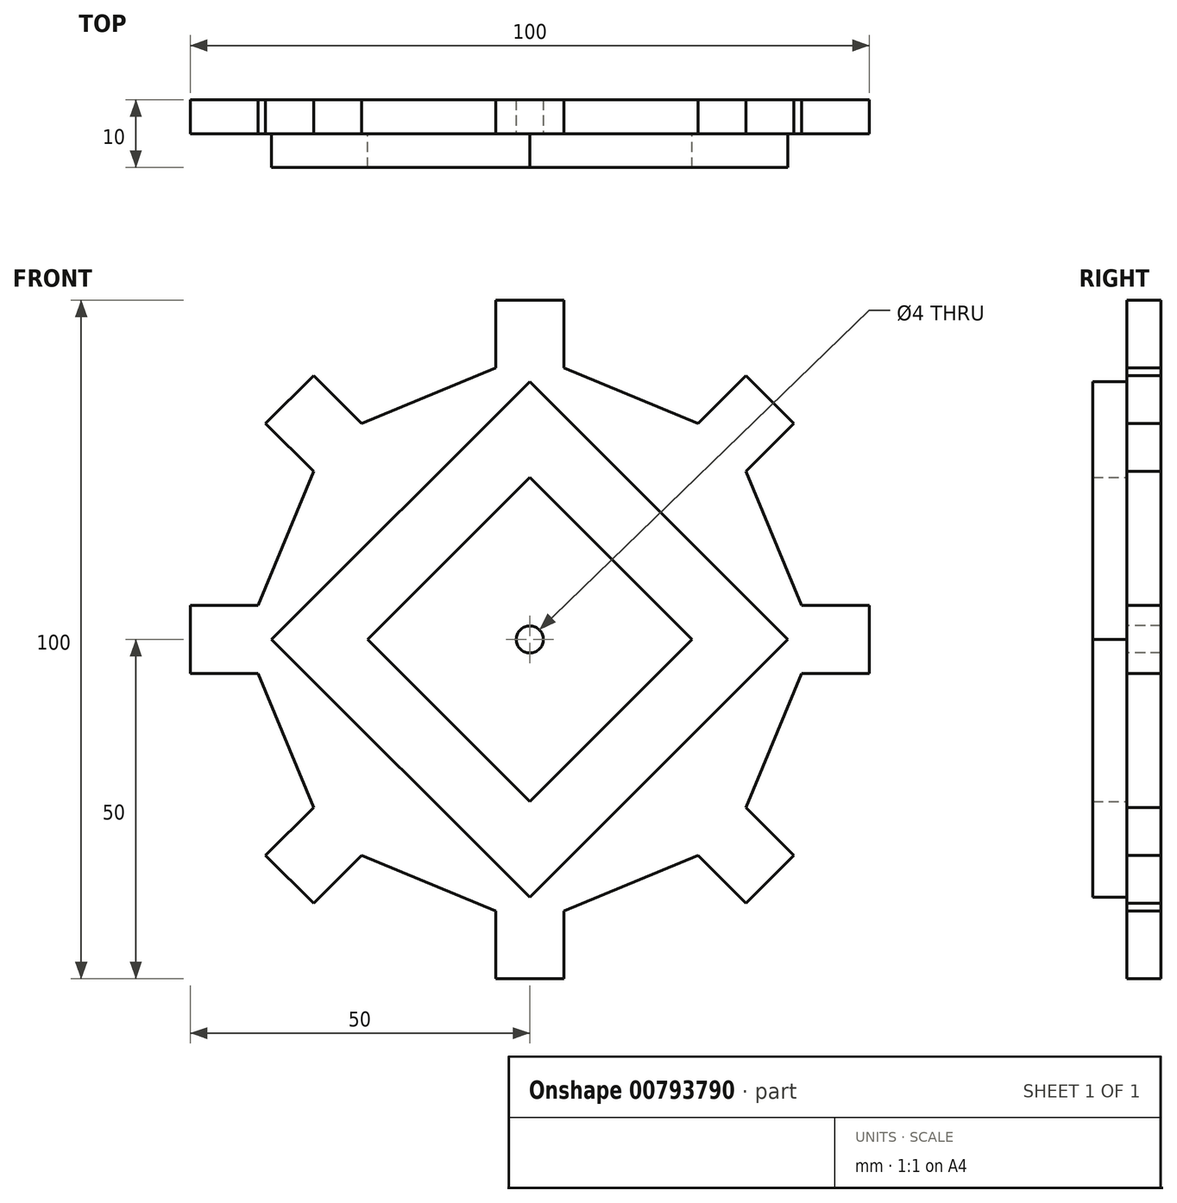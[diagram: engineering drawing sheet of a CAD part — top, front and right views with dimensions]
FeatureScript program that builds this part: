
annotation { "Feature Type Name" : "Feature", "Feature Type Description" : "" }
export const myFeature = defineFeature(function(context is Context, id is Id, definition is map)
    precondition{}
    {
        {
            var Q0;
            Q0=qCreatedBy(makeId("Front.planeOp"),FACE);
            var sketch = newSketch(context, id + "F0", { "sketchPlane" : qUnion([Q0])});
            skLineSegment(sketch, "E0.bottom", {"start": v(5, -50) * mm, "end": v(-5, -50) * mm});
            skLineSegment(sketch, "E0.top", {"start": v(5, 50) * mm, "end": v(-5, 50) * mm});
            skLineSegment(sketch, "E0.left", {"start": v(5, -50) * mm, "end": v(5, 50) * mm});
            skLineSegment(sketch, "E0.right", {"start": v(-5, -50) * mm, "end": v(-5, 50) * mm});
            skPoint(sketch, "E0.middle", {"position": v(0, 0) * mm});
            skLineSegment(sketch, "E1.bottom", {"start": v(50, -5) * mm, "end": v(-50, -5) * mm});
            skLineSegment(sketch, "E1.top", {"start": v(50, 5) * mm, "end": v(-50, 5) * mm});
            skLineSegment(sketch, "E1.left", {"start": v(50, -5) * mm, "end": v(50, 5) * mm});
            skLineSegment(sketch, "E1.right", {"start": v(-50, -5) * mm, "end": v(-50, 5) * mm});
            skLineSegment(sketch, "E2", {"start": v(-5, -5) * mm, "end": v(5, 5) * mm});
            skLineSegment(sketch, "E3", {"start": v(0, 0) * mm, "end": v(-3.54, -3.54) * mm});
            skLineSegment(sketch, "E4", {"start": v(0, 0) * mm, "end": v(3.54, 3.54) * mm});
            skLineSegment(sketch, "E5", {"start": v(3.54, 3.54) * mm, "end": v(-31.82, 38.9) * mm});
            skLineSegment(sketch, "E6", {"start": v(-31.82, 38.9) * mm, "end": v(-38.9, 31.82) * mm});
            skLineSegment(sketch, "E7", {"start": v(-38.9, 31.82) * mm, "end": v(-3.54, -3.54) * mm});
            skLineSegment(sketch, "E8.MirrorCS", {"start": v(3.54, 3.54) * mm, "end": v(38.9, -31.82) * mm});
            skLineSegment(sketch, "E9.MirrorCS", {"start": v(31.82, -38.9) * mm, "end": v(-3.54, -3.54) * mm});
            skLineSegment(sketch, "E10.MirrorCS", {"start": v(38.9, -31.82) * mm, "end": v(31.82, -38.9) * mm});
            skLineSegment(sketch, "E11", {"start": v(-5, 5) * mm, "end": v(5, -5) * mm});
            skLineSegment(sketch, "E12", {"start": v(0, 0) * mm, "end": v(-3.54, 3.54) * mm});
            skLineSegment(sketch, "E13", {"start": v(0, 0) * mm, "end": v(3.54, -3.54) * mm});
            skLineSegment(sketch, "E14", {"start": v(3.54, -3.54) * mm, "end": v(-31.82, -38.9) * mm});
            skLineSegment(sketch, "E15", {"start": v(-31.82, -38.9) * mm, "end": v(-38.9, -31.82) * mm});
            skLineSegment(sketch, "E16", {"start": v(-38.9, -31.82) * mm, "end": v(-3.54, 3.54) * mm});
            skLineSegment(sketch, "E17.MirrorCS", {"start": v(3.54, -3.54) * mm, "end": v(38.9, 31.82) * mm});
            skLineSegment(sketch, "E18.MirrorCS", {"start": v(31.82, 38.9) * mm, "end": v(-3.54, 3.54) * mm});
            skLineSegment(sketch, "E19.MirrorCS", {"start": v(38.9, 31.82) * mm, "end": v(31.82, 38.9) * mm});
            skLineSegment(sketch, "E20", {"start": v(-5, 50) * mm, "end": v(-5, 40) * mm});
            skLineSegment(sketch, "E21", {"start": v(-5, 40) * mm, "end": v(5, 40) * mm});
            skLineSegment(sketch, "E22", {"start": v(-38.9, 31.82) * mm, "end": v(-31.82, 24.75) * mm});
            skLineSegment(sketch, "E23", {"start": v(-31.82, 24.75) * mm, "end": v(-24.75, 31.82) * mm});
            skLineSegment(sketch, "E24", {"start": v(-50, -5) * mm, "end": v(-40, -5) * mm});
            skLineSegment(sketch, "E25", {"start": v(-40, -5) * mm, "end": v(-40, 5) * mm});
            skLineSegment(sketch, "E26", {"start": v(-31.82, -38.9) * mm, "end": v(-24.75, -31.82) * mm});
            skLineSegment(sketch, "E27", {"start": v(-24.75, -31.82) * mm, "end": v(-31.82, -24.75) * mm});
            skLineSegment(sketch, "E28", {"start": v(5, -50) * mm, "end": v(5, -40) * mm});
            skLineSegment(sketch, "E29", {"start": v(5, -40) * mm, "end": v(-5, -40) * mm});
            skLineSegment(sketch, "E30", {"start": v(38.9, -31.82) * mm, "end": v(31.82, -24.75) * mm});
            skLineSegment(sketch, "E31", {"start": v(31.82, -24.75) * mm, "end": v(24.75, -31.82) * mm});
            skLineSegment(sketch, "E32", {"start": v(50, -5) * mm, "end": v(40, -5) * mm});
            skLineSegment(sketch, "E33", {"start": v(40, -5) * mm, "end": v(40, 5) * mm});
            skLineSegment(sketch, "E34", {"start": v(38.9, 31.82) * mm, "end": v(31.82, 24.75) * mm});
            skLineSegment(sketch, "E35", {"start": v(31.82, 24.75) * mm, "end": v(24.75, 31.82) * mm});
            skLineSegment(sketch, "E36", {"start": v(24.75, 31.82) * mm, "end": v(5, 40) * mm});
            skLineSegment(sketch, "E37", {"start": v(-5, 40) * mm, "end": v(-24.75, 31.82) * mm});
            skLineSegment(sketch, "E38", {"start": v(-31.82, 24.75) * mm, "end": v(-40, 5) * mm});
            skLineSegment(sketch, "E39", {"start": v(-40, -5) * mm, "end": v(-31.82, -24.75) * mm});
            skLineSegment(sketch, "E40", {"start": v(-24.75, -31.82) * mm, "end": v(-5, -40) * mm});
            skLineSegment(sketch, "E41", {"start": v(5, -40) * mm, "end": v(24.75, -31.82) * mm});
            skLineSegment(sketch, "E42", {"start": v(31.82, -24.75) * mm, "end": v(40, -5) * mm});
            skLineSegment(sketch, "E43", {"start": v(40, 5) * mm, "end": v(31.82, 24.75) * mm});
            skSolve(sketch);
        }
        {
            var Q0;
            {var subQ3=sQuery(id+"F0.wireOp",EDGE,"E40");Q0=makeQuery(id+"F0.imprint","IMPRINT",FACE,{"disambiguationData":[TD([[makeQuery(id+"F0.imprint","IMPRINT",EDGE,{"derivedFrom":subQ3}),1.0]])]});}
            var Q1;
            {var subQ3=sQuery(id+"F0.wireOp",EDGE,"E37");Q1=makeQuery(id+"F0.imprint","IMPRINT",FACE,{"disambiguationData":[TD([[makeQuery(id+"F0.imprint","IMPRINT",EDGE,{"derivedFrom":subQ3}),1.0]])]});}
            var Q2;
            {var subQ3=sQuery(id+"F0.wireOp",EDGE,"E36");Q2=makeQuery(id+"F0.imprint","IMPRINT",FACE,{"disambiguationData":[TD([[makeQuery(id+"F0.imprint","IMPRINT",EDGE,{"derivedFrom":subQ3}),1.0]])]});}
            var Q3;
            {var subQ0=sQuery(id+"F0.wireOp",EDGE,"E15");Q3=makeQuery(id+"F0.imprint","IMPRINT",FACE,{"disambiguationData":[TD([[makeQuery(id+"F0.imprint","IMPRINT",EDGE,{"derivedFrom":subQ0}),-1.0]])]});}
            var Q4;
            {var subQ0=sQuery(id+"F0.wireOp",EDGE,"E19.MirrorCS");Q4=makeQuery(id+"F0.imprint","IMPRINT",FACE,{"disambiguationData":[TD([[makeQuery(id+"F0.imprint","IMPRINT",EDGE,{"derivedFrom":subQ0}),1.0]])]});}
            var Q5;
            {var subQ0=sQuery(id+"F0.wireOp",EDGE,"E41");Q5=makeQuery(id+"F0.imprint","IMPRINT",FACE,{"disambiguationData":[TD([[makeQuery(id+"F0.imprint","IMPRINT",EDGE,{"derivedFrom":subQ0}),1.0]])]});}
            var Q6;
            {var subQ0=sQuery(id+"F0.wireOp",EDGE,"E10.MirrorCS");Q6=makeQuery(id+"F0.imprint","IMPRINT",FACE,{"disambiguationData":[TD([[makeQuery(id+"F0.imprint","IMPRINT",EDGE,{"derivedFrom":subQ0}),-1.0]])]});}
            var Q7;
            {var subQ3=sQuery(id+"F0.wireOp",EDGE,"E39");Q7=makeQuery(id+"F0.imprint","IMPRINT",FACE,{"disambiguationData":[TD([[makeQuery(id+"F0.imprint","IMPRINT",EDGE,{"derivedFrom":subQ3}),1.0]])]});}
            var Q8;
            {var subQ3=sQuery(id+"F0.wireOp",EDGE,"E23");Q8=makeQuery(id+"F0.imprint","IMPRINT",FACE,{"disambiguationData":[TD([[makeQuery(id+"F0.imprint","IMPRINT",EDGE,{"derivedFrom":subQ3}),-1.0]])]});}
            var Q9;
            {var subQ0=sQuery(id+"F0.wireOp",EDGE,"E6");Q9=makeQuery(id+"F0.imprint","IMPRINT",FACE,{"disambiguationData":[TD([[makeQuery(id+"F0.imprint","IMPRINT",EDGE,{"derivedFrom":subQ0}),1.0]])]});}
            var Q10;
            {var subQ3=sQuery(id+"F0.wireOp",EDGE,"E38");Q10=makeQuery(id+"F0.imprint","IMPRINT",FACE,{"disambiguationData":[TD([[makeQuery(id+"F0.imprint","IMPRINT",EDGE,{"derivedFrom":subQ3}),1.0]])]});}
            var Q11;
            {var subQ0=sQuery(id+"F0.wireOp",EDGE,"E1.right");Q11=makeQuery(id+"F0.imprint","IMPRINT",FACE,{"disambiguationData":[TD([[makeQuery(id+"F0.imprint","IMPRINT",EDGE,{"derivedFrom":subQ0}),-1.0]])]});}
            var Q12;
            {var subQ0=sQuery(id+"F0.wireOp",EDGE,"E7");var subQ1=sQuery(id+"F0.wireOp",EDGE,"E0.right");var subQ2=makeQuery(id+"F0.imprint","INTERSECT",VERTEX,{"derivedFrom":[subQ1,subQ0]});Q12=makeQuery(id+"F0.imprint","IMPRINT",FACE,{"disambiguationData":[TD([[makeQuery(id+"F0.imprint","IMPRINT",EDGE,{"disambiguationData":[TD([[subQ2,1.0]])],"derivedFrom":subQ0}),-1.0]])]});}
            var Q13;
            {var subQ0=sQuery(id+"F0.wireOp",EDGE,"E1.left");Q13=makeQuery(id+"F0.imprint","IMPRINT",FACE,{"disambiguationData":[TD([[makeQuery(id+"F0.imprint","IMPRINT",EDGE,{"derivedFrom":subQ0}),1.0]])]});}
            var Q14;
            {var subQ0=sQuery(id+"F0.wireOp",EDGE,"E17.MirrorCS");var subQ1=sQuery(id+"F0.wireOp",EDGE,"E0.left");var subQ2=makeQuery(id+"F0.imprint","INTERSECT",VERTEX,{"derivedFrom":[subQ1,subQ0]});Q14=makeQuery(id+"F0.imprint","IMPRINT",FACE,{"disambiguationData":[TD([[makeQuery(id+"F0.imprint","IMPRINT",EDGE,{"disambiguationData":[TD([[subQ2,-1.0]])],"derivedFrom":subQ1}),-1.0]])]});}
            var Q15;
            {var subQ0=sQuery(id+"F0.wireOp",EDGE,"E0.top");Q15=makeQuery(id+"F0.imprint","IMPRINT",FACE,{"disambiguationData":[TD([[makeQuery(id+"F0.imprint","IMPRINT",EDGE,{"derivedFrom":subQ0}),1.0]])]});}
            var Q16;
            {var subQ3=sQuery(id+"F0.wireOp",EDGE,"E17.MirrorCS");var subQ6=sQuery(id+"F0.wireOp",EDGE,"E0.left");var subQ9=makeQuery(id+"F0.imprint","INTERSECT",VERTEX,{"derivedFrom":[subQ6,subQ3]});Q16=makeQuery(id+"F0.imprint","IMPRINT",FACE,{"disambiguationData":[TD([[makeQuery(id+"F0.imprint","IMPRINT",EDGE,{"disambiguationData":[TD([[subQ9,-1.0]])],"derivedFrom":subQ6}),1.0]])]});}
            var Q17;
            {var subQ7=sQuery(id+"F0.wireOp",EDGE,"E29");Q17=makeQuery(id+"F0.imprint","IMPRINT",FACE,{"disambiguationData":[TD([[makeQuery(id+"F0.imprint","IMPRINT",EDGE,{"derivedFrom":subQ7}),-1.0]])]});}
            var Q18;
            {var subQ0=sQuery(id+"F0.wireOp",EDGE,"E0.bottom");Q18=makeQuery(id+"F0.imprint","IMPRINT",FACE,{"disambiguationData":[TD([[makeQuery(id+"F0.imprint","IMPRINT",EDGE,{"derivedFrom":subQ0}),-1.0]])]});}
            var Q19;
            {var subQ0=sQuery(id+"F0.wireOp",EDGE,"E9.MirrorCS");var subQ1=sQuery(id+"F0.wireOp",EDGE,"E0.left");var subQ2=makeQuery(id+"F0.imprint","INTERSECT",VERTEX,{"derivedFrom":[subQ1,subQ0]});Q19=makeQuery(id+"F0.imprint","IMPRINT",FACE,{"disambiguationData":[TD([[makeQuery(id+"F0.imprint","IMPRINT",EDGE,{"disambiguationData":[TD([[subQ2,-1.0]])],"derivedFrom":subQ0}),-1.0]])]});}
            var Q20;
            {var subQ7=sQuery(id+"F0.wireOp",EDGE,"E33");Q20=makeQuery(id+"F0.imprint","IMPRINT",FACE,{"disambiguationData":[TD([[makeQuery(id+"F0.imprint","IMPRINT",EDGE,{"derivedFrom":subQ7}),1.0]])]});}
            var Q21;
            {var subQ0=sQuery(id+"F0.wireOp",EDGE,"E8.MirrorCS");var subQ1=sQuery(id+"F0.wireOp",EDGE,"E0.left");var subQ2=makeQuery(id+"F0.imprint","INTERSECT",VERTEX,{"derivedFrom":[subQ1,subQ0]});Q21=makeQuery(id+"F0.imprint","IMPRINT",FACE,{"disambiguationData":[TD([[makeQuery(id+"F0.imprint","IMPRINT",EDGE,{"disambiguationData":[TD([[subQ2,-1.0]])],"derivedFrom":subQ0}),1.0]])]});}
            var Q22;
            {var subQ0=sQuery(id+"F0.wireOp",EDGE,"E31");Q22=makeQuery(id+"F0.imprint","IMPRINT",FACE,{"disambiguationData":[TD([[makeQuery(id+"F0.imprint","IMPRINT",EDGE,{"derivedFrom":subQ0}),-1.0]])]});}
            var Q23;
            {var subQ0=sQuery(id+"F0.wireOp",EDGE,"E14");var subQ1=sQuery(id+"F0.wireOp",EDGE,"E1.bottom");var subQ2=makeQuery(id+"F0.imprint","INTERSECT",VERTEX,{"derivedFrom":[subQ1,subQ0]});Q23=makeQuery(id+"F0.imprint","IMPRINT",FACE,{"disambiguationData":[TD([[makeQuery(id+"F0.imprint","IMPRINT",EDGE,{"disambiguationData":[TD([[subQ2,-1.0]])],"derivedFrom":subQ1}),1.0]])]});}
            var Q24;
            {var subQ3=sQuery(id+"F0.wireOp",EDGE,"E35");Q24=makeQuery(id+"F0.imprint","IMPRINT",FACE,{"disambiguationData":[TD([[makeQuery(id+"F0.imprint","IMPRINT",EDGE,{"derivedFrom":subQ3}),1.0]])]});}
            var Q25;
            {var subQ7=sQuery(id+"F0.wireOp",EDGE,"E25");Q25=makeQuery(id+"F0.imprint","IMPRINT",FACE,{"disambiguationData":[TD([[makeQuery(id+"F0.imprint","IMPRINT",EDGE,{"derivedFrom":subQ7}),-1.0]])]});}
            var Q26;
            {var subQ0=sQuery(id+"F0.wireOp",EDGE,"E1.bottom");var subQ5=sQuery(id+"F0.wireOp",EDGE,"E9.MirrorCS");var subQ6=makeQuery(id+"F0.imprint","INTERSECT",VERTEX,{"derivedFrom":[subQ0,subQ5]});Q26=makeQuery(id+"F0.imprint","IMPRINT",FACE,{"disambiguationData":[TD([[makeQuery(id+"F0.imprint","IMPRINT",EDGE,{"disambiguationData":[TD([[subQ6,1.0]])],"derivedFrom":subQ5}),1.0]])]});}
            var Q27;
            {var subQ3=sQuery(id+"F0.wireOp",EDGE,"E1.bottom");var subQ5=sQuery(id+"F0.wireOp",EDGE,"E8.MirrorCS");var subQ6=makeQuery(id+"F0.imprint","INTERSECT",VERTEX,{"derivedFrom":[subQ3,subQ5]});Q27=makeQuery(id+"F0.imprint","IMPRINT",FACE,{"disambiguationData":[TD([[makeQuery(id+"F0.imprint","IMPRINT",EDGE,{"disambiguationData":[TD([[subQ6,1.0]])],"derivedFrom":subQ5}),-1.0]])]});}
            var Q28;
            {var subQ3=sQuery(id+"F0.wireOp",EDGE,"E42");Q28=makeQuery(id+"F0.imprint","IMPRINT",FACE,{"disambiguationData":[TD([[makeQuery(id+"F0.imprint","IMPRINT",EDGE,{"derivedFrom":subQ3}),1.0]])]});}
            var Q29;
            {var subQ3=sQuery(id+"F0.wireOp",EDGE,"E43");Q29=makeQuery(id+"F0.imprint","IMPRINT",FACE,{"disambiguationData":[TD([[makeQuery(id+"F0.imprint","IMPRINT",EDGE,{"derivedFrom":subQ3}),1.0]])]});}
            var Q30;
            {var subQ3=sQuery(id+"F0.wireOp",EDGE,"E1.bottom");var subQ7=sQuery(id+"F0.wireOp",EDGE,"E14");var subQ9=makeQuery(id+"F0.imprint","INTERSECT",VERTEX,{"derivedFrom":[subQ3,subQ7]});Q30=makeQuery(id+"F0.imprint","IMPRINT",FACE,{"disambiguationData":[TD([[makeQuery(id+"F0.imprint","IMPRINT",EDGE,{"disambiguationData":[TD([[subQ9,-1.0]])],"derivedFrom":subQ3}),-1.0]])]});}
            var Q31;
            {var subQ7=sQuery(id+"F0.wireOp",EDGE,"E21");Q31=makeQuery(id+"F0.imprint","IMPRINT",FACE,{"disambiguationData":[TD([[makeQuery(id+"F0.imprint","IMPRINT",EDGE,{"derivedFrom":subQ7}),-1.0]])]});}
            var Q32;
            {var subQ0=sQuery(id+"F0.wireOp",EDGE,"E7");var subQ1=sQuery(id+"F0.wireOp",EDGE,"E0.right");var subQ2=makeQuery(id+"F0.imprint","INTERSECT",VERTEX,{"derivedFrom":[subQ1,subQ0]});Q32=makeQuery(id+"F0.imprint","IMPRINT",FACE,{"disambiguationData":[TD([[makeQuery(id+"F0.imprint","IMPRINT",EDGE,{"disambiguationData":[TD([[subQ2,-1.0]])],"derivedFrom":subQ1}),1.0]])]});}
            var Q33;
            {var subQ0=sQuery(id+"F0.wireOp",EDGE,"E1.top");var subQ5=sQuery(id+"F0.wireOp",EDGE,"E7");var subQ6=makeQuery(id+"F0.imprint","INTERSECT",VERTEX,{"derivedFrom":[subQ0,subQ5]});Q33=makeQuery(id+"F0.imprint","IMPRINT",FACE,{"disambiguationData":[TD([[makeQuery(id+"F0.imprint","IMPRINT",EDGE,{"disambiguationData":[TD([[subQ6,-1.0]])],"derivedFrom":subQ5}),1.0]])]});}
            var Q34;
            {var subQ0=sQuery(id+"F0.wireOp",EDGE,"E5");var subQ1=sQuery(id+"F0.wireOp",EDGE,"E1.top");var subQ2=makeQuery(id+"F0.imprint","INTERSECT",VERTEX,{"derivedFrom":[subQ1,subQ0]});Q34=makeQuery(id+"F0.imprint","IMPRINT",FACE,{"disambiguationData":[TD([[makeQuery(id+"F0.imprint","IMPRINT",EDGE,{"disambiguationData":[TD([[subQ2,-1.0]])],"derivedFrom":subQ1}),-1.0]])]});}
            var Q35;
            {var subQ0=sQuery(id+"F0.wireOp",EDGE,"E7");var subQ1=sQuery(id+"F0.wireOp",EDGE,"E0.right");var subQ2=makeQuery(id+"F0.imprint","INTERSECT",VERTEX,{"derivedFrom":[subQ1,subQ0]});Q35=makeQuery(id+"F0.imprint","IMPRINT",FACE,{"disambiguationData":[TD([[makeQuery(id+"F0.imprint","IMPRINT",EDGE,{"disambiguationData":[TD([[subQ2,-1.0]])],"derivedFrom":subQ1}),-1.0]])]});}
            var Q36;
            {var subQ3=sQuery(id+"F0.wireOp",EDGE,"E1.top");var subQ5=sQuery(id+"F0.wireOp",EDGE,"E5");var subQ6=makeQuery(id+"F0.imprint","INTERSECT",VERTEX,{"derivedFrom":[subQ3,subQ5]});Q36=makeQuery(id+"F0.imprint","IMPRINT",FACE,{"disambiguationData":[TD([[makeQuery(id+"F0.imprint","IMPRINT",EDGE,{"disambiguationData":[TD([[subQ6,-1.0]])],"derivedFrom":subQ5}),-1.0]])]});}
            var Q37;
            {var subQ0=sQuery(id+"F0.wireOp",EDGE,"E5");var subQ1=sQuery(id+"F0.wireOp",EDGE,"E0.right");var subQ2=makeQuery(id+"F0.imprint","INTERSECT",VERTEX,{"derivedFrom":[subQ1,subQ0]});Q37=makeQuery(id+"F0.imprint","IMPRINT",FACE,{"disambiguationData":[TD([[makeQuery(id+"F0.imprint","IMPRINT",EDGE,{"disambiguationData":[TD([[subQ2,1.0]])],"derivedFrom":subQ0}),1.0]])]});}
            var Q38;
            {var subQ3=sQuery(id+"F0.wireOp",EDGE,"E27");Q38=makeQuery(id+"F0.imprint","IMPRINT",FACE,{"disambiguationData":[TD([[makeQuery(id+"F0.imprint","IMPRINT",EDGE,{"derivedFrom":subQ3}),-1.0]])]});}
            var Q39;
            {var subQ5=sQuery(id+"F0.wireOp",EDGE,"E5");var subQ6=sQuery(id+"F0.wireOp",EDGE,"E1.top");var subQ7=makeQuery(id+"F0.imprint","INTERSECT",VERTEX,{"derivedFrom":[subQ6,subQ5]});Q39=makeQuery(id+"F0.imprint","IMPRINT",FACE,{"disambiguationData":[TD([[makeQuery(id+"F0.imprint","IMPRINT",EDGE,{"disambiguationData":[TD([[subQ7,-1.0]])],"derivedFrom":subQ6}),1.0]])]});}
            var Q40;
            {var subQ1=sQuery(id+"F0.wireOp",EDGE,"E1.top");var subQ3=sQuery(id+"F0.wireOp",EDGE,"E18.MirrorCS");var subQ4=makeQuery(id+"F0.imprint","INTERSECT",VERTEX,{"derivedFrom":[subQ1,subQ3]});Q40=makeQuery(id+"F0.imprint","IMPRINT",FACE,{"disambiguationData":[TD([[makeQuery(id+"F0.imprint","IMPRINT",EDGE,{"disambiguationData":[TD([[subQ4,-1.0]])],"derivedFrom":subQ1}),1.0]])]});}
            var Q41;
            {var subQ0=sQuery(id+"F0.wireOp",EDGE,"E14");var subQ1=sQuery(id+"F0.wireOp",EDGE,"E1.bottom");var subQ2=makeQuery(id+"F0.imprint","INTERSECT",VERTEX,{"derivedFrom":[subQ1,subQ0]});Q41=makeQuery(id+"F0.imprint","IMPRINT",FACE,{"disambiguationData":[TD([[makeQuery(id+"F0.imprint","IMPRINT",EDGE,{"disambiguationData":[TD([[subQ2,1.0]])],"derivedFrom":subQ1}),-1.0]])]});}
            var Q42;
            {var subQ1=sQuery(id+"F0.wireOp",EDGE,"E0.right");var subQ3=sQuery(id+"F0.wireOp",EDGE,"E16");var subQ4=makeQuery(id+"F0.imprint","INTERSECT",VERTEX,{"derivedFrom":[subQ1,subQ3]});Q42=makeQuery(id+"F0.imprint","IMPRINT",FACE,{"disambiguationData":[TD([[makeQuery(id+"F0.imprint","IMPRINT",EDGE,{"disambiguationData":[TD([[subQ4,-1.0]])],"derivedFrom":subQ1}),-1.0]])]});}
            var Q43;
            {var subQ0=sQuery(id+"F0.wireOp",EDGE,"E17.MirrorCS");var subQ1=sQuery(id+"F0.wireOp",EDGE,"E0.left");var subQ2=makeQuery(id+"F0.imprint","INTERSECT",VERTEX,{"derivedFrom":[subQ1,subQ0]});Q43=makeQuery(id+"F0.imprint","IMPRINT",FACE,{"disambiguationData":[TD([[makeQuery(id+"F0.imprint","IMPRINT",EDGE,{"disambiguationData":[TD([[subQ2,1.0]])],"derivedFrom":subQ1}),1.0]])]});}
            var Q44;
            {var subQ1=sQuery(id+"F0.wireOp",EDGE,"E1.bottom");var subQ3=sQuery(id+"F0.wireOp",EDGE,"E9.MirrorCS");var subQ4=makeQuery(id+"F0.imprint","INTERSECT",VERTEX,{"derivedFrom":[subQ1,subQ3]});Q44=makeQuery(id+"F0.imprint","IMPRINT",FACE,{"disambiguationData":[TD([[makeQuery(id+"F0.imprint","IMPRINT",EDGE,{"disambiguationData":[TD([[subQ4,-1.0]])],"derivedFrom":subQ1}),-1.0]])]});}
            var Q45;
            {var subQ0=sQuery(id+"F0.wireOp",EDGE,"E8.MirrorCS");var subQ1=sQuery(id+"F0.wireOp",EDGE,"E0.left");var subQ2=makeQuery(id+"F0.imprint","INTERSECT",VERTEX,{"derivedFrom":[subQ1,subQ0]});Q45=makeQuery(id+"F0.imprint","IMPRINT",FACE,{"disambiguationData":[TD([[makeQuery(id+"F0.imprint","IMPRINT",EDGE,{"disambiguationData":[TD([[subQ2,-1.0]])],"derivedFrom":subQ1}),1.0]])]});}
            var Q46;
            {var subQ0=sQuery(id+"F0.wireOp",EDGE,"E5");var subQ1=sQuery(id+"F0.wireOp",EDGE,"E1.top");var subQ2=makeQuery(id+"F0.imprint","INTERSECT",VERTEX,{"derivedFrom":[subQ1,subQ0]});Q46=makeQuery(id+"F0.imprint","IMPRINT",FACE,{"disambiguationData":[TD([[makeQuery(id+"F0.imprint","IMPRINT",EDGE,{"disambiguationData":[TD([[subQ2,1.0]])],"derivedFrom":subQ1}),1.0]])]});}
            var Q47;
            {var subQ0=sQuery(id+"F0.wireOp",EDGE,"E7");var subQ1=sQuery(id+"F0.wireOp",EDGE,"E0.right");var subQ2=makeQuery(id+"F0.imprint","INTERSECT",VERTEX,{"derivedFrom":[subQ1,subQ0]});Q47=makeQuery(id+"F0.imprint","IMPRINT",FACE,{"disambiguationData":[TD([[makeQuery(id+"F0.imprint","IMPRINT",EDGE,{"disambiguationData":[TD([[subQ2,1.0]])],"derivedFrom":subQ1}),-1.0]])]});}
            extrude(context, id + "F1", {"entities" : qUnion([Q0, Q1, Q2, Q3, Q4, Q5, Q6, Q7, Q8, Q9, Q10, Q11, Q12, Q13, Q14, Q15, Q16, Q17, Q18, Q19, Q20, Q21, Q22, Q23, Q24, Q25, Q26, Q27, Q28, Q29, Q30, Q31, Q32, Q33, Q34, Q35, Q36, Q37, Q38, Q39, Q40, Q41, Q42, Q43, Q44, Q45, Q46, Q47]), "depth" : 5 * mm, "offsetDistance" : 25 * mm});
        }
        {
            var Q0;
            Q0=makeQuery(id+"F1.opExtrude","CAP_FACE",FACE,{"disambiguationData":[OSD([sQuery(id+"F0.wireOp",EDGE,"E0.bottom"),sQuery(id+"F0.wireOp",EDGE,"E0.top"),sQuery(id+"F0.wireOp",EDGE,"E0.left"),sQuery(id+"F0.wireOp",EDGE,"E0.right"),sQuery(id+"F0.wireOp",EDGE,"E1.bottom"),sQuery(id+"F0.wireOp",EDGE,"E1.top"),sQuery(id+"F0.wireOp",EDGE,"E1.left"),sQuery(id+"F0.wireOp",EDGE,"E1.right"),sQuery(id+"F0.wireOp",EDGE,"E5"),sQuery(id+"F0.wireOp",EDGE,"E6"),sQuery(id+"F0.wireOp",EDGE,"E7"),sQuery(id+"F0.wireOp",EDGE,"E8.MirrorCS"),sQuery(id+"F0.wireOp",EDGE,"E9.MirrorCS"),sQuery(id+"F0.wireOp",EDGE,"E10.MirrorCS"),sQuery(id+"F0.wireOp",EDGE,"E14"),sQuery(id+"F0.wireOp",EDGE,"E15"),sQuery(id+"F0.wireOp",EDGE,"E16"),sQuery(id+"F0.wireOp",EDGE,"E17.MirrorCS"),sQuery(id+"F0.wireOp",EDGE,"E18.MirrorCS"),sQuery(id+"F0.wireOp",EDGE,"E19.MirrorCS"),sQuery(id+"F0.wireOp",EDGE,"E36"),sQuery(id+"F0.wireOp",EDGE,"E37"),sQuery(id+"F0.wireOp",EDGE,"E38"),sQuery(id+"F0.wireOp",EDGE,"E39"),sQuery(id+"F0.wireOp",EDGE,"E40"),sQuery(id+"F0.wireOp",EDGE,"E41"),sQuery(id+"F0.wireOp",EDGE,"E42"),sQuery(id+"F0.wireOp",EDGE,"E43")])],"isStart":false});
            var sketch = newSketch(context, id + "F2", { "sketchPlane" : qUnion([Q0])});
            skLineSegment(sketch, "E44", {"start": v(-50, -5) * mm, "end": v(50, -5) * mm, "construction": true});
            skLineSegment(sketch, "E45", {"start": v(50, 5) * mm, "end": v(-50, 5) * mm, "construction": true});
            skLineSegment(sketch, "E46", {"start": v(-5, 50) * mm, "end": v(-5, -50) * mm, "construction": true});
            skLineSegment(sketch, "E47", {"start": v(5, -50) * mm, "end": v(5, 50) * mm, "construction": true});
            skLineSegment(sketch, "E48", {"start": v(-31.82, 38.9) * mm, "end": v(-5, 12.07) * mm, "construction": true});
            skLineSegment(sketch, "E49", {"start": v(-38.9, 31.82) * mm, "end": v(-12.07, 5) * mm, "construction": true});
            skLineSegment(sketch, "E50", {"start": v(-31.82, -38.9) * mm, "end": v(-5, -12.07) * mm, "construction": true});
            skLineSegment(sketch, "E51", {"start": v(-38.9, -31.82) * mm, "end": v(-12.07, -5) * mm, "construction": true});
            skLineSegment(sketch, "E52", {"start": v(31.82, -38.9) * mm, "end": v(5, -12.07) * mm, "construction": true});
            skLineSegment(sketch, "E53", {"start": v(38.9, -31.82) * mm, "end": v(12.07, -5) * mm, "construction": true});
            skLineSegment(sketch, "E54", {"start": v(38.9, 31.82) * mm, "end": v(12.07, 5) * mm, "construction": true});
            skLineSegment(sketch, "E55", {"start": v(31.82, 38.9) * mm, "end": v(5, 12.07) * mm, "construction": true});
            skLineSegment(sketch, "E56", {"start": v(-50, 0) * mm, "end": v(-38, 0) * mm});
            skLineSegment(sketch, "E57", {"start": v(0, 50) * mm, "end": v(0, 38) * mm});
            skLineSegment(sketch, "E58", {"start": v(50, 0) * mm, "end": v(38, 0) * mm});
            skLineSegment(sketch, "E59", {"start": v(0, -50) * mm, "end": v(0, -38) * mm});
            skLineSegment(sketch, "E60", {"start": v(0, -38) * mm, "end": v(-38, 0) * mm});
            skLineSegment(sketch, "E61", {"start": v(-38, 0) * mm, "end": v(0, 38) * mm});
            skLineSegment(sketch, "E62", {"start": v(38, 0) * mm, "end": v(0, 38) * mm});
            skLineSegment(sketch, "E63", {"start": v(38, 0) * mm, "end": v(0, -38) * mm});
            skLineSegment(sketch, "E64", {"start": v(0, -38) * mm, "end": v(7.07, -30.93) * mm});
            skLineSegment(sketch, "E65", {"start": v(7.07, -30.93) * mm, "end": v(0, -23.86) * mm});
            skLineSegment(sketch, "E66", {"start": v(-38, 0) * mm, "end": v(-30.93, -7.07) * mm});
            skLineSegment(sketch, "E67", {"start": v(-30.93, -7.07) * mm, "end": v(-23.86, 0) * mm});
            skLineSegment(sketch, "E68", {"start": v(0, 38) * mm, "end": v(-7.07, 30.93) * mm});
            skLineSegment(sketch, "E69", {"start": v(-7.07, 30.93) * mm, "end": v(0, 23.86) * mm});
            skLineSegment(sketch, "E70", {"start": v(38, 0) * mm, "end": v(30.93, 7.07) * mm});
            skLineSegment(sketch, "E71", {"start": v(30.93, 7.07) * mm, "end": v(23.86, 0) * mm});
            skLineSegment(sketch, "E72", {"start": v(23.86, 0) * mm, "end": v(0, -23.86) * mm});
            skLineSegment(sketch, "E73", {"start": v(-23.86, 0) * mm, "end": v(0, -23.86) * mm});
            skLineSegment(sketch, "E74", {"start": v(-23.86, 0) * mm, "end": v(0, 23.86) * mm});
            skLineSegment(sketch, "E75", {"start": v(23.86, 0) * mm, "end": v(0, 23.86) * mm});
            skCircle(sketch, "E76", {"center": v(0, 0) * mm, "radius": 2 * mm});
            skSolve(sketch);
        }
        {
            var Q0;
            Q0 = qSketchRegion(id + "F2", true);
            extrude(context, id + "F3", {"entities" : qUnion([Q0]), "operationType" : NewBodyOperationType.ADD, "depth" : 5 * mm, "offsetDistance" : 25 * mm});
        }
        {
            var Q0;
            Q0=makeQuery(id+"F2.imprint","IMPRINT",FACE,{"disambiguationData":[TD([[makeQuery(id+"F2.imprint","IMPRINT",EDGE,{"derivedFrom":sQuery(id+"F2.wireOp",EDGE,"E76")}),1.0]])]});
            extrude(context, id + "F4", {"entities" : qUnion([Q0]), "operationType" : NewBodyOperationType.REMOVE, "oppositeDirection" : true, "depth" : 25 * mm, "offsetDistance" : 25 * mm});
        }
    });
